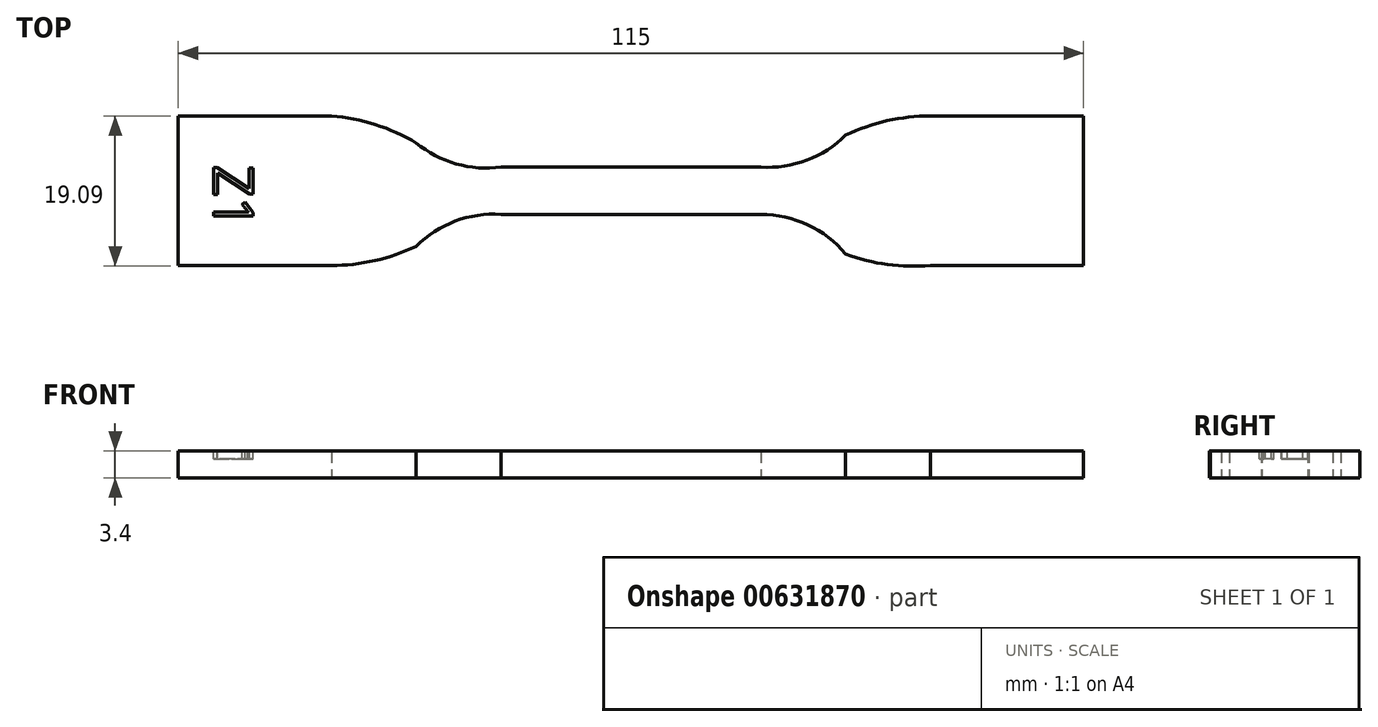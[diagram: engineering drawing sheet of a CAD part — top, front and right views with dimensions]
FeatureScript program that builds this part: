
annotation { "Feature Type Name" : "Feature", "Feature Type Description" : "" }
export const myFeature = defineFeature(function(context is Context, id is Id, definition is map)
    precondition{}
    {
        {
            var Q0;
            Q0=qCreatedBy(makeId("Top.planeOp"),FACE);
            var sketch = newSketch(context, id + "F0", { "sketchPlane" : qUnion([Q0])});
            skLineSegment(sketch, "E0", {"start": v(-33.87, 19.78) * mm, "end": v(-33.87, 0.78) * mm});
            skLineSegment(sketch, "E1", {"start": v(-33.87, 0.78) * mm, "end": v(-14.43, 0.78) * mm});
            skLineSegment(sketch, "E2", {"start": v(-33.87, 19.78) * mm, "end": v(-14.43, 19.78) * mm});
            skLineSegment(sketch, "E3", {"start": v(61.69, 19.78) * mm, "end": v(81.13, 19.78) * mm});
            skLineSegment(sketch, "E4", {"start": v(81.13, 19.78) * mm, "end": v(81.13, 0.78) * mm});
            skLineSegment(sketch, "E5", {"start": v(81.13, 0.78) * mm, "end": v(61.69, 0.78) * mm});
            skLineSegment(sketch, "E6", {"start": v(7.13, 13.28) * mm, "end": v(40.13, 13.28) * mm});
            skLineSegment(sketch, "E7", {"start": v(7.13, 7.28) * mm, "end": v(40.13, 7.28) * mm});
            skArc(sketch, "E8", {"start": v(-3.65, 16.36) * mm, "mid": v(-8.85, 18.69) * mm, "end": v(-14.43, 19.78) * mm});
            skArc(sketch, "E9", {"start": v(-3.65, 16.36) * mm, "mid": v(1.42, 13.7) * mm, "end": v(7.13, 13.28) * mm});
            skArc(sketch, "E10", {"start": v(-14.43, 0.78) * mm, "mid": v(-8.9, 1.4) * mm, "end": v(-3.65, 3.22) * mm});
            skArc(sketch, "E11", {"start": v(7.13, 7.28) * mm, "mid": v(1.3, 6.41) * mm, "end": v(-3.65, 3.22) * mm});
            skArc(sketch, "E12", {"start": v(40.13, 13.28) * mm, "mid": v(45.95, 14.15) * mm, "end": v(50.9, 17.34) * mm});
            skArc(sketch, "E13", {"start": v(61.69, 19.78) * mm, "mid": v(56.16, 19.16) * mm, "end": v(50.9, 17.34) * mm});
            skArc(sketch, "E14", {"start": v(50.9, 2.21) * mm, "mid": v(46.08, 5.95) * mm, "end": v(40.13, 7.28) * mm});
            skArc(sketch, "E15", {"start": v(50.9, 2.21) * mm, "mid": v(56.22, 0.9) * mm, "end": v(61.69, 0.78) * mm});
            skSolve(sketch);
        }
        {
            var Q0;
            Q0=qSketchRegion(id+"F0",true);
            extrude(context, id + "F1", {"entities" : qUnion([Q0]), "depth" : 3.4 * mm, "offsetDistance" : 25 * mm});
        }
        {
            var Q0;
            Q0=makeQuery(id+"F1.opExtrude","CAP_FACE",FACE,{"disambiguationData":[OSD([sQuery(id+"F0.wireOp",EDGE,"E0"),sQuery(id+"F0.wireOp",EDGE,"E1"),sQuery(id+"F0.wireOp",EDGE,"E2"),sQuery(id+"F0.wireOp",EDGE,"E3"),sQuery(id+"F0.wireOp",EDGE,"E4"),sQuery(id+"F0.wireOp",EDGE,"E5"),sQuery(id+"F0.wireOp",EDGE,"E6"),sQuery(id+"F0.wireOp",EDGE,"E7"),sQuery(id+"F0.wireOp",EDGE,"E8"),sQuery(id+"F0.wireOp",EDGE,"E9"),sQuery(id+"F0.wireOp",EDGE,"E10"),sQuery(id+"F0.wireOp",EDGE,"E11"),sQuery(id+"F0.wireOp",EDGE,"E12"),sQuery(id+"F0.wireOp",EDGE,"E13"),sQuery(id+"F0.wireOp",EDGE,"E14"),sQuery(id+"F0.wireOp",EDGE,"E15")])],"isStart":false});
            var sketch = newSketch(context, id + "F2", { "sketchPlane" : qUnion([Q0])});
            skText(sketch, "E16", { "text": "Z1", "fontName": "OpenSans-Regular.ttf"});
            const initialGuessF2  = {"E16": [-0.02939, 0.01353, 0, -1, 0.00508]};
            skSetInitialGuess(sketch, initialGuessF2);
            skSolve(sketch);
        }
        {
            var Q0;
            Q0=qSketchRegion(id+"F2",true);
            extrude(context, id + "F3", {"entities" : qUnion([Q0]), "operationType" : NewBodyOperationType.REMOVE, "oppositeDirection" : true, "depth" : 1 * mm, "offsetDistance" : 25 * mm});
        }
    });
